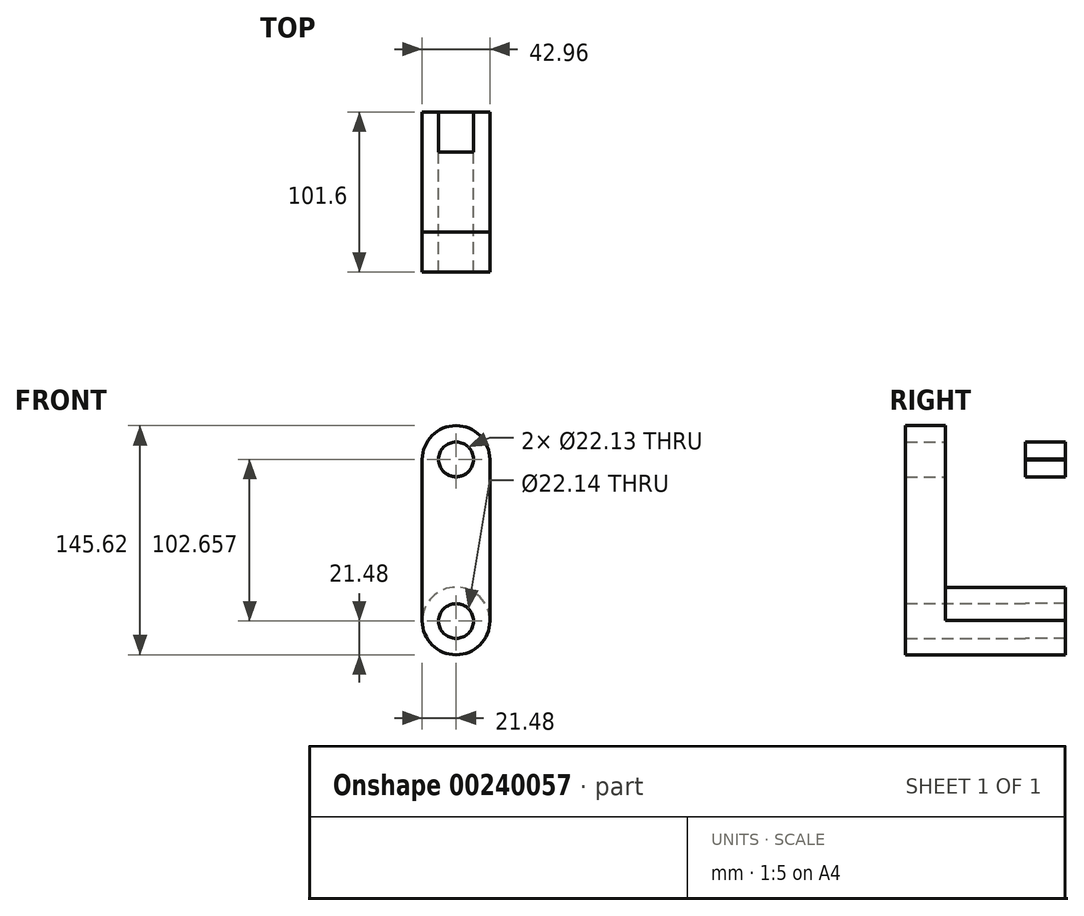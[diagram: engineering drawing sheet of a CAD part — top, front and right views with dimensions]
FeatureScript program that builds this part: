
annotation { "Feature Type Name" : "Feature", "Feature Type Description" : "" }
export const myFeature = defineFeature(function(context is Context, id is Id, definition is map)
    precondition{}
    {
        {
            var Q0;
            Q0=qCreatedBy(makeId("Front.planeOp"),FACE);
            var sketch = newSketch(context, id + "F0", { "sketchPlane" : qUnion([Q0])});
            skCircle(sketch, "E0", {"center": v(0, 0) * mm, "radius": 11.06 * mm});
            skArc(sketch, "E1", {"start": v(-21.48, 0) * mm, "mid": v(0, -21.48) * mm, "end": v(21.48, 0) * mm});
            skLineSegment(sketch, "E2", {"start": v(0, 0) * mm, "end": v(0, 102.66) * mm, "construction": true});
            skLineSegment(sketch, "E3", {"start": v(0, 51.33) * mm, "end": v(-45.93, 51.33) * mm, "construction": true});
            skArc(sketch, "E4.MirrorC", {"start": v(21.48, 0) * mm, "mid": v(0, -21.48) * mm, "end": v(-21.48, 0) * mm});
            skArc(sketch, "E5.MirrorC", {"start": v(21.48, 102.66) * mm, "mid": v(0, 124.14) * mm, "end": v(-21.48, 102.66) * mm});
            skCircle(sketch, "E6.MirrorC", {"center": v(0, 102.66) * mm, "radius": 11.06 * mm});
            skLineSegment(sketch, "E7", {"start": v(-21.48, 0) * mm, "end": v(-21.48, 102.66) * mm});
            skLineSegment(sketch, "E8", {"start": v(21.48, 0) * mm, "end": v(21.48, 102.66) * mm});
            skSolve(sketch);
        }
        {
            var Q0;
            Q0=makeQuery(id+"F0.imprint","IMPRINT",FACE,{"disambiguationData":[TD([[makeQuery(id+"F0.imprint","IMPRINT",EDGE,{"derivedFrom":sQuery(id+"F0.wireOp",EDGE,"E0")}),-1.0]])]});
            extrude(context, id + "F1", {"entities" : qUnion([Q0]), "depth" : 25.4 * mm});
        }
        {
            var Q0;
            Q0=makeQuery(id+"F1.opExtrude","CAP_FACE",FACE,{"disambiguationData":[OSD([sQuery(id+"F0.wireOp",EDGE,"E0"),sQuery(id+"F0.wireOp",EDGE,"E4.MirrorC"),sQuery(id+"F0.wireOp",EDGE,"E5.MirrorC"),sQuery(id+"F0.wireOp",EDGE,"E6.MirrorC"),sQuery(id+"F0.wireOp",EDGE,"E7"),sQuery(id+"F0.wireOp",EDGE,"E8")])],"isStart":true});
            var sketch = newSketch(context, id + "F2", { "sketchPlane" : qUnion([Q0])});
            skCircle(sketch, "E9", {"center": v(0, 0) * mm, "radius": 21.48 * mm});
            skSolve(sketch);
        }
        {
            var Q0;
            Q0=makeQuery(id+"F2.imprint","IMPRINT",FACE,{"disambiguationData":[TD([[makeQuery(id+"F2.imprint","IMPRINT",EDGE,{"derivedFrom":makeQuery(id+"F1.opExtrude","CAP_EDGE",EDGE,{"disambiguationData":[OSD([sQuery(id+"F0.wireOp",EDGE,"E0")])],"isStart":true})}),1.0]])]});
            extrude(context, id + "F3", {"entities" : qUnion([Q0]), "operationType" : NewBodyOperationType.ADD, "depth" : 50.8 * mm});
        }
        {
            var Q0;
            Q0=makeQuery(id+"F3.opExtrude","CAP_FACE",FACE,{"disambiguationData":[OSD([sQuery(id+"F0.wireOp",EDGE,"E0"),sQuery(id+"F0.wireOp",EDGE,"E4.MirrorC"),sQuery(id+"F0.wireOp",EDGE,"E7"),sQuery(id+"F0.wireOp",EDGE,"E8"),sQuery(id+"F2.wireOp",EDGE,"E9")])],"isStart":false});
            var sketch = newSketch(context, id + "F4", { "sketchPlane" : qUnion([Q0])});
            skCircle(sketch, "E10", {"center": v(0, 0) * mm, "radius": 21.48 * mm});
            skLineSegment(sketch, "E11", {"start": v(0, 0) * mm, "end": v(0, 102.67) * mm, "construction": true});
            skLineSegment(sketch, "E12", {"start": v(0, 51.33) * mm, "end": v(-46.95, 51.33) * mm, "construction": true});
            skPoint(sketch, "E12.endSnap0", {"position": v(0, 51.33) * mm});
            skCircle(sketch, "E13", {"center": v(0, 0) * mm, "radius": 11.07 * mm});
            skCircle(sketch, "E14.MirrorC", {"center": v(0, 102.67) * mm, "radius": 21.48 * mm});
            skCircle(sketch, "E15.MirrorC", {"center": v(0, 102.67) * mm, "radius": 11.07 * mm});
            skLineSegment(sketch, "E16", {"start": v(-21.48, 0.25) * mm, "end": v(-21.48, 102.91) * mm});
            skLineSegment(sketch, "E17", {"start": v(21.48, 0.25) * mm, "end": v(21.48, 102.91) * mm});
            skSolve(sketch);
        }
        {
            var Q0;
            {var subQ3=sQuery(id+"F4.wireOp",EDGE,"E16");var subQ5=sQuery(id+"F4.wireOp",EDGE,"E14.MirrorC");var subQ6=makeQuery(id+"F4.imprint","INTERSECT",VERTEX,{"disambiguationData":[OD(1.0)],"derivedFrom":[subQ5,subQ3]});Q0=makeQuery(id+"F4.imprint","IMPRINT",FACE,{"disambiguationData":[TD([[makeQuery(id+"F4.imprint","IMPRINT",EDGE,{"disambiguationData":[TD([[subQ6,1.0]])],"derivedFrom":subQ5}),1.0]])]});}
            var Q1;
            Q1=makeQuery(id+"F4.imprint","IMPRINT",FACE,{"disambiguationData":[TD([[makeQuery(id+"F4.imprint","IMPRINT",EDGE,{"derivedFrom":sQuery(id+"F4.wireOp",EDGE,"E15.MirrorC")}),1.0]])]});
            var Q2;
            Q2=makeQuery(id+"F4.imprint","IMPRINT",FACE,{"disambiguationData":[TD([[makeQuery(id+"F4.imprint","IMPRINT",EDGE,{"derivedFrom":sQuery(id+"F4.wireOp",EDGE,"E13")}),-1.0]])]});
            extrude(context, id + "F5", {"entities" : qUnion([Q0, Q1, Q2]), "operationType" : NewBodyOperationType.ADD, "depth" : 25.4 * mm});
        }
    });
